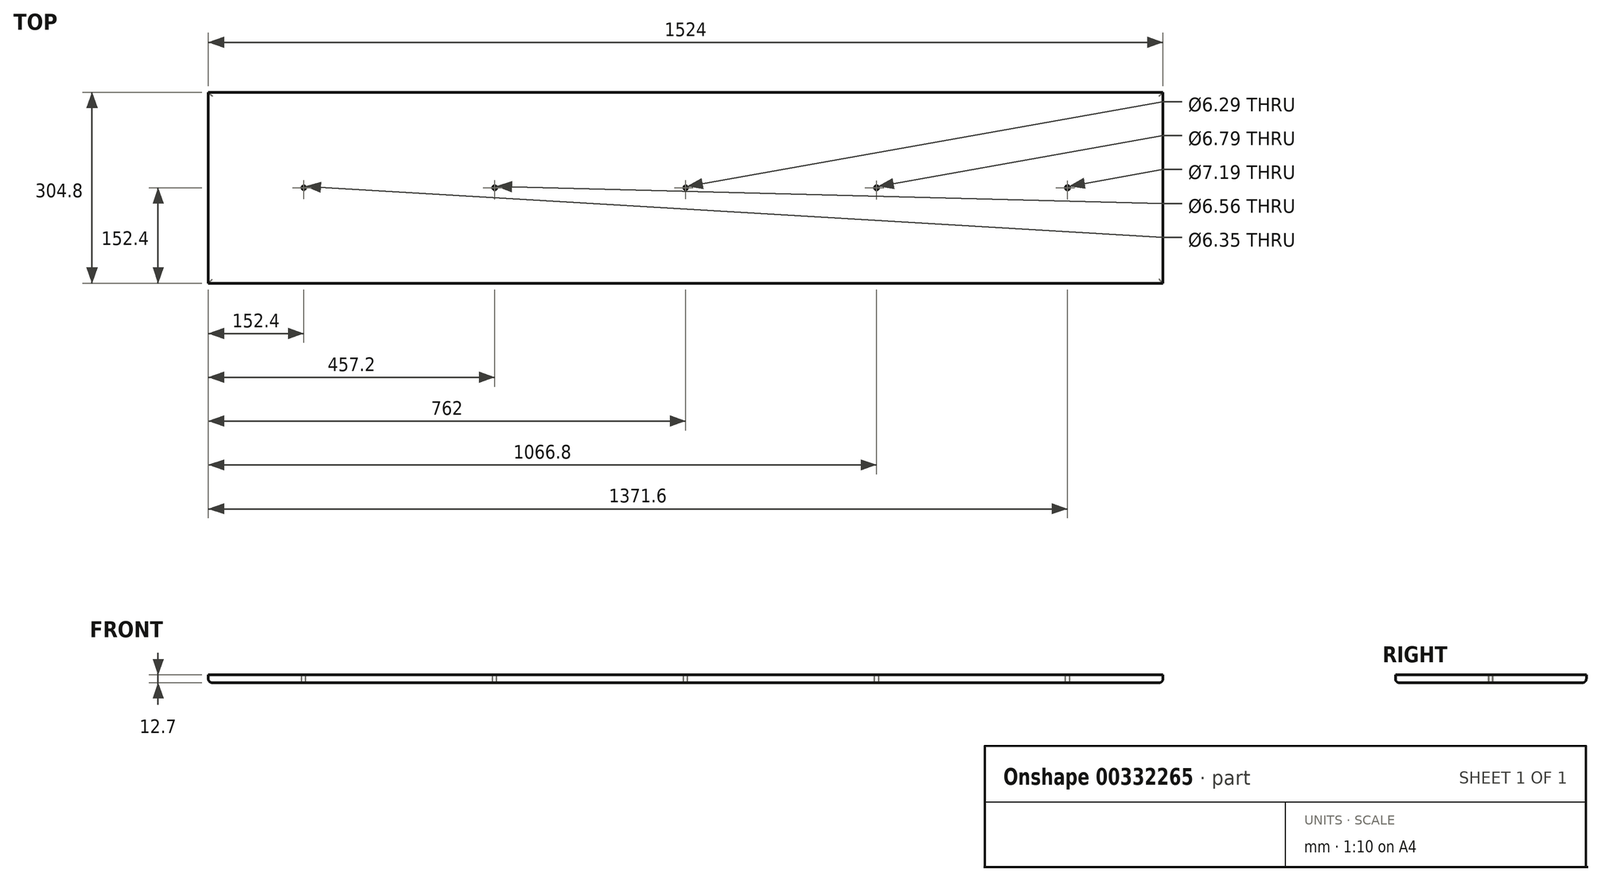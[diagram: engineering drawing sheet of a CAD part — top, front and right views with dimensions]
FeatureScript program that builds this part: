
annotation { "Feature Type Name" : "Feature", "Feature Type Description" : "" }
export const myFeature = defineFeature(function(context is Context, id is Id, definition is map)
    precondition{}
    {
        {
            var Q0;
            Q0=qCreatedBy(makeId("Top.planeOp"),FACE);
            var sketch = newSketch(context, id + "F0", { "sketchPlane" : qUnion([Q0])});
            skLineSegment(sketch, "E0.bottom", {"start": v(762, -152.4) * mm, "end": v(-762, -152.4) * mm});
            skLineSegment(sketch, "E0.top", {"start": v(762, 152.4) * mm, "end": v(-762, 152.4) * mm});
            skLineSegment(sketch, "E0.left", {"start": v(762, -152.4) * mm, "end": v(762, 152.4) * mm});
            skLineSegment(sketch, "E0.right", {"start": v(-762, -152.4) * mm, "end": v(-762, 152.4) * mm});
            skPoint(sketch, "E0.middle", {"position": v(0, 0) * mm});
            skSolve(sketch);
        }
        {
            var Q0;
            Q0=qCreatedBy(makeId("Top.planeOp"),FACE);
            var sketch = newSketch(context, id + "F1", { "sketchPlane" : qUnion([Q0])});
            skCircle(sketch, "E1", {"center": v(0, 0) * mm, "radius": 3.15 * mm});
            skCircle(sketch, "E2", {"center": v(304.8, 0) * mm, "radius": 3.4 * mm});
            skCircle(sketch, "E3", {"center": v(609.6, 0) * mm, "radius": 3.6 * mm});
            skCircle(sketch, "E4", {"center": v(-304.8, 0) * mm, "radius": 3.28 * mm});
            skCircle(sketch, "E5", {"center": v(-609.6, 0) * mm, "radius": 3.18 * mm});
            skSolve(sketch);
        }
        {
            var Q0;
            Q0 = qSketchRegion(id + "F0", true);
            extrude(context, id + "F2", {"entities" : qUnion([Q0]), "depth" : 12.7 * mm});
        }
        {
            var Q0;
            Q0 = qSketchRegion(id + "F1", true);
            extrude(context, id + "F3", {"entities" : qUnion([Q0]), "operationType" : NewBodyOperationType.REMOVE, "oppositeDirection" : true, "depth" : 25.4 * mm, "hasSecondDirection" : true, "secondDirectionOppositeDirection" : false, "secondDirectionDepth" : 25.4 * mm});
        }
        {
            var Q0;
            Q0=makeQuery(id+"F2.opExtrude","CAP_EDGE",EDGE,{"disambiguationData":[OSD([sQuery(id+"F0.wireOp",EDGE,"E0.bottom")])],"isStart":true});
            var Q1;
            Q1=makeQuery(id+"F2.opExtrude","CAP_EDGE",EDGE,{"disambiguationData":[OSD([sQuery(id+"F0.wireOp",EDGE,"E0.left")])],"isStart":true});
            var Q2;
            Q2=makeQuery(id+"F2.opExtrude","CAP_EDGE",EDGE,{"disambiguationData":[OSD([sQuery(id+"F0.wireOp",EDGE,"E0.right")])],"isStart":true});
            var Q3;
            Q3=makeQuery(id+"F2.opExtrude","CAP_EDGE",EDGE,{"disambiguationData":[OSD([sQuery(id+"F0.wireOp",EDGE,"E0.top")])],"isStart":true});
            fillet(context, id + "F4", {"entities" : qUnion([Q0, Q1, Q2, Q3]), "radius" : 6.35 * mm, "tangentPropagation" : true, "allowEdgeOverflow" : false});
        }
    });
